FCSTD DOCUMENT  (FreeCAD 0.20RUnknown)
Label: plate-3inch-2x2
License: All rights reserved
LicenseURL: http://en.wikipedia.org/wiki/All_rights_reserved
objects: Sketcher::SketchObject×1, PartDesign::Body×1
note: 2 computed .brp shape members not serialized (recipe doc carries the construction recipe); baked Part::Feature solids carry a one-line shape summary decoded from their .brp

FEATURE [Sketcher::SketchObject] Sketch
  FullyConstrained = false
  MapMode = 5
  Support = -> [XY_Plane]
  sketch-geometry (14):
    g0: Circle CenterX=-35.0377 CenterY=40.1593 CenterZ=0 NormalX=0 NormalY=0 NormalZ=1 AngleXU=0 Radius=12.725
    g1: Circle CenterX=40.4423 CenterY=40.1593 CenterZ=0 NormalX=0 NormalY=0 NormalZ=1 AngleXU=0 Radius=12.725
    g2: Circle CenterX=-35.0377 CenterY=-35.3207 CenterZ=0 NormalX=0 NormalY=0 NormalZ=1 AngleXU=0 Radius=12.725
    g3: Circle CenterX=40.4423 CenterY=-35.3207 CenterZ=0 NormalX=0 NormalY=0 NormalZ=1 AngleXU=0 Radius=12.725
    g4: ArcOfCircle CenterX=-70.5977 CenterY=75.7193 CenterZ=0 NormalX=0 NormalY=0 NormalZ=1 AngleXU=0 Radius=2.54 StartAngle=1.5708 EndAngle=3.14159
    g5: LineSegment StartX=-70.5977 StartY=78.2593 StartZ=0 EndX=76.0023 EndY=78.2593 EndZ=0
    g6: ArcOfCircle CenterX=76.0023 CenterY=75.7193 CenterZ=0 NormalX=0 NormalY=0 NormalZ=1 AngleXU=0 Radius=2.54 StartAngle=0 EndAngle=1.5708
    g7: LineSegment StartX=78.5423 StartY=75.7193 StartZ=0 EndX=78.5423 EndY=-70.8807 EndZ=0
    g8: ArcOfCircle CenterX=76.0023 CenterY=-70.8807 CenterZ=0 NormalX=0 NormalY=0 NormalZ=1 AngleXU=0 Radius=2.54 StartAngle=4.71239 EndAngle=6.28319
    g9: LineSegment StartX=76.0023 StartY=-73.4207 StartZ=0 EndX=-70.5977 EndY=-73.4207 EndZ=0
    g10: ArcOfCircle CenterX=-70.5977 CenterY=-70.8807 CenterZ=0 NormalX=0 NormalY=0 NormalZ=1 AngleXU=0 Radius=2.54 StartAngle=3.14159 EndAngle=4.71239
    g11: LineSegment StartX=-73.1377 StartY=-70.8807 StartZ=0 EndX=-73.1377 EndY=75.7193 EndZ=0
    g12: GeomPoint X=-73.1377 Y=78.2593 Z=0
    g13: GeomPoint X=78.5423 Y=-73.4207 Z=0
  constraints (34):
    c: Diameter(g3) = 25.45
    c: Diameter(g2) = 25.45
    c: Diameter(g0) = 25.45
    c: Diameter(g1) = 25.45
    c: Tangent(g4,g5) = 1.5708
    c: Tangent(g5,g6) = 1.5708
    c: Tangent(g6,g7) = 1.5708
    c: Tangent(g7,g8) = 1.5708
    c: Tangent(g8,g9) = 1.5708
    c: Tangent(g9,g10) = 1.5708
    c: Tangent(g10,g11) = 1.5708
    c: Tangent(g11,g4) = 1.5708
    c: Horizontal(g5)
    c: Horizontal(g9)
    c: Vertical(g7)
    c: Vertical(g11)
    c: Equal(g4,g6)
    c: Equal(g6,g8)
    c: Equal(g8,g10)
    c: PointOnObject(g12,g5)
    c: PointOnObject(g12,g11)
    c: PointOnObject(g13,g7)
    c: PointOnObject(g13,g9)
    c: Diameter(g4) = 5.08
    c: Distance(g7) = 146.6
    c: Distance(g5) = 146.6
    c: Distance(g0,g11) = 38.1
    c: Distance(g0,g5) = 38.1
    c: Distance(g1,g5) = 38.1
    c: Distance(g1,g7) = 38.1
    c: Distance(g2,g9) = 38.1
    c: Distance(g2,g11) = 38.1
    c: Distance(g3,g9) = 38.1
    c: Distance(g3,g7) = 38.1
FEATURE [PartDesign::Body] Body
  Group = -> [Sketch]
  Origin = -> Origin
